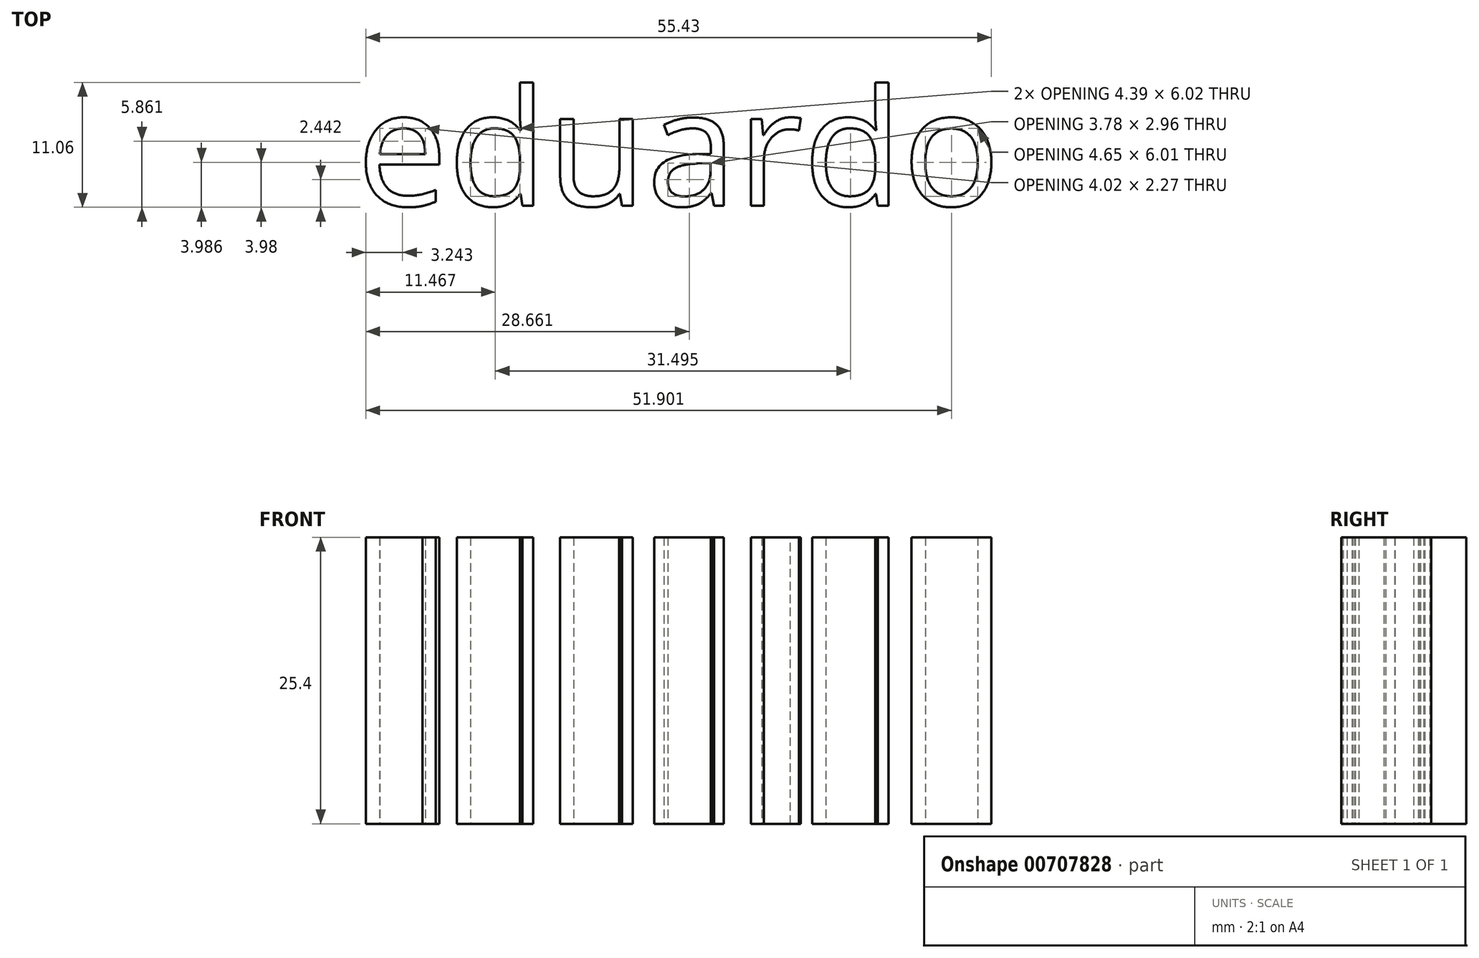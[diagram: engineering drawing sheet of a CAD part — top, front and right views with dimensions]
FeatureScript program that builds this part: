
annotation { "Feature Type Name" : "Feature", "Feature Type Description" : "" }
export const myFeature = defineFeature(function(context is Context, id is Id, definition is map)
    precondition{}
    {
        {
            var Q0;
            Q0=qCreatedBy(makeId("Top.planeOp"),FACE);
            var sketch = newSketch(context, id + "F0", { "sketchPlane" : qUnion([Q0])});
            skText(sketch, "E0", { "text": "eduardo\n", "fontName": "OpenSans-Regular.ttf"});
            const initialGuessF0  = {"E0": [-0.0572, -0.04018, 1, 0, 0.01035]};
            skSetInitialGuess(sketch, initialGuessF0);
            skSolve(sketch);
        }
        {
            var Q0;
            Q0 = qSketchRegion(id + "F0", true);
            extrude(context, id + "F1", {"entities" : qUnion([Q0]), "depth" : 25.4 * mm, "offsetDistance" : 25.4 * mm});
        }
    });
